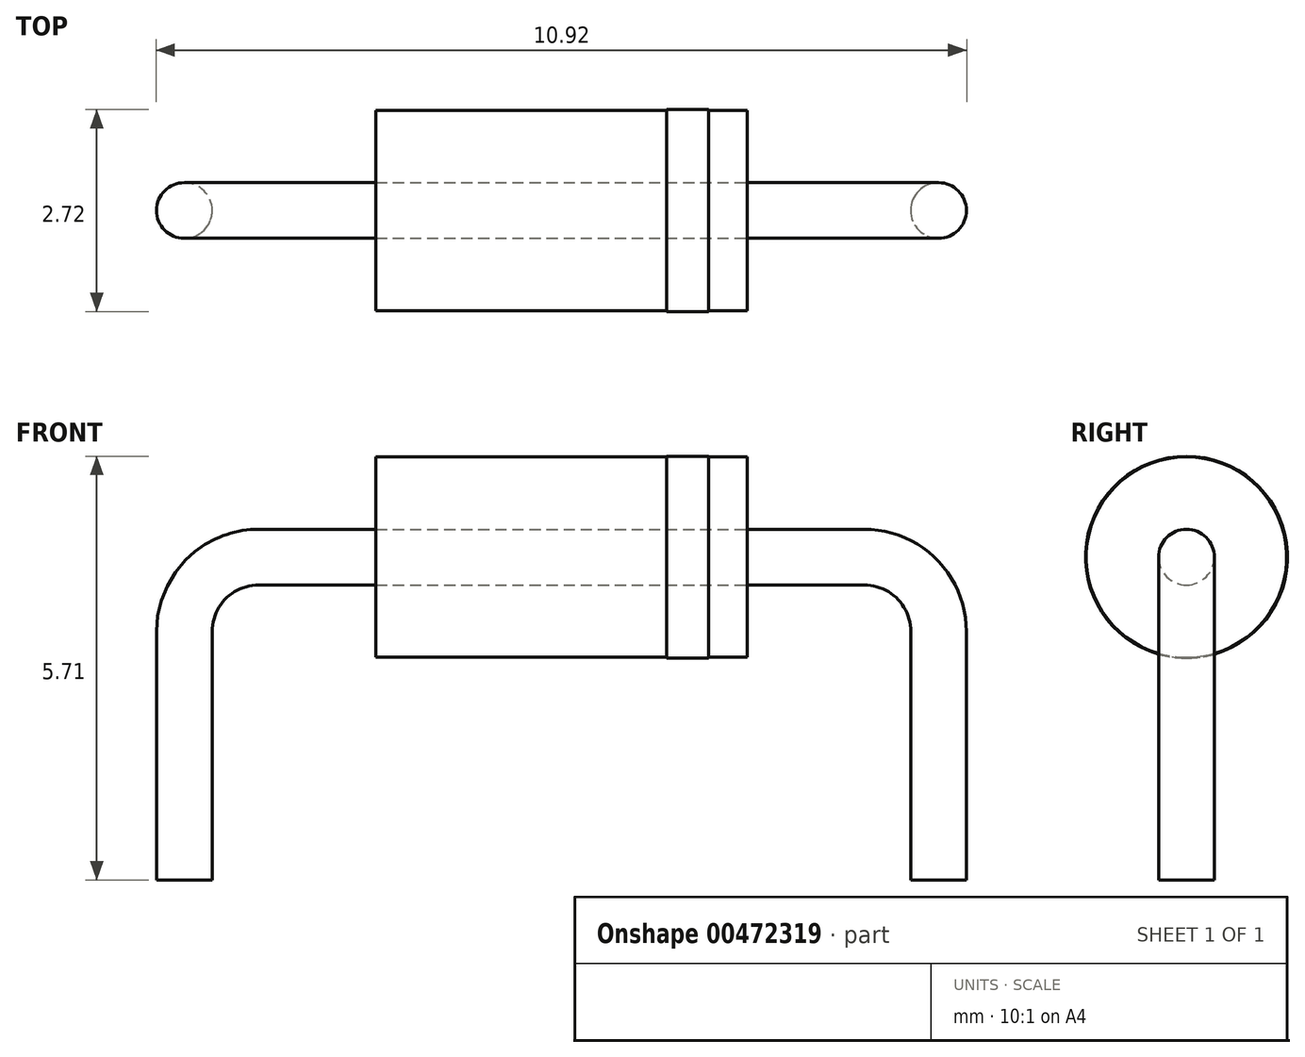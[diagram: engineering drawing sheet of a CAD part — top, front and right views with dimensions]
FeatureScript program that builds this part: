
annotation { "Feature Type Name" : "Feature", "Feature Type Description" : "" }
export const myFeature = defineFeature(function(context is Context, id is Id, definition is map)
    precondition{}
    {
        {
            var Q0;
            Q0=qCreatedBy(makeId("Front.planeOp"),FACE);
            var sketch = newSketch(context, id + "F0", { "sketchPlane" : qUnion([Q0])});
            skLineSegment(sketch, "E0", {"start": v(-5.08, 0) * mm, "end": v(-5.08, 3.35) * mm});
            skLineSegment(sketch, "E1", {"start": v(-4.08, 4.35) * mm, "end": v(4.08, 4.35) * mm});
            skLineSegment(sketch, "E2", {"start": v(5.08, 3.35) * mm, "end": v(5.08, 0) * mm});
            skPoint(sketch, "E3.visualSharp", {"position": v(-5.08, 4.35) * mm});
            skArc(sketch, "E3.filletArc", {"start": v(-4.08, 4.35) * mm, "mid": v(-4.79, 4.06) * mm, "end": v(-5.08, 3.35) * mm});
            skPoint(sketch, "E4.visualSharp", {"position": v(5.08, 4.35) * mm});
            skArc(sketch, "E4.filletArc", {"start": v(5.08, 3.35) * mm, "mid": v(4.79, 4.06) * mm, "end": v(4.08, 4.35) * mm});
            skSolve(sketch);
        }
        {
            var Q0;
            Q0=qCreatedBy(makeId("Top.planeOp"),FACE);
            var sketch = newSketch(context, id + "F1", { "sketchPlane" : qUnion([Q0])});
            skCircle(sketch, "E5", {"center": v(-5.08, 0) * mm, "radius": 0.38 * mm});
            skSolve(sketch);
        }
        {
            var Q0;
            Q0=qSketchRegion(id+"F1",true);
            var Q1;
            Q1=qConstructionFilter(qBodyType(qCreatedBy(id+"F0",EDGE),BodyType.WIRE),ConstructionObject.NO);
            sweep(context, id + "F2", {"profiles" : qUnion([Q0]), "path" : qUnion([Q1])});
        }
        {
            var Q0;
            Q0=qCreatedBy(makeId("Right.planeOp"),FACE);
            var sketch = newSketch(context, id + "F3", { "sketchPlane" : qUnion([Q0])});
            skCircle(sketch, "E6", {"center": v(0, 4.35) * mm, "radius": 1.35 * mm});
            skSolve(sketch);
        }
        {
            var Q0;
            Q0=makeQuery(id+"F3.imprint","IMPRINT",FACE,{"disambiguationData":[TD([[makeQuery(id+"F3.imprint","IMPRINT",EDGE,{"derivedFrom":sQuery(id+"F3.wireOp",EDGE,"E6")}),1.0]])]});
            extrude(context, id + "F4", {"entities" : qUnion([Q0]), "oppositeDirection" : true, "depth" : 2.5 * mm, "hasSecondDirection" : true, "secondDirectionOppositeDirection" : false, "secondDirectionDepth" : 2.5 * mm});
        }
        {
            var Q0;
            Q0=makeQuery(id+"F4.opExtrude","CAP_FACE",FACE,{"disambiguationData":[OSD([sQuery(id+"F3.wireOp",EDGE,"E6")])],"isStart":true});
            var sketch = newSketch(context, id + "F5", { "sketchPlane" : qUnion([Q0])});
            skCircle(sketch, "E7", {"center": v(0, 4.35) * mm, "radius": 1.36 * mm});
            skSolve(sketch);
        }
        {
            var Q0;
            Q0=qSketchRegion(id+"F5",true);
            extrude(context, id + "F6", {"entities" : qUnion([Q0]), "oppositeDirection" : true, "depth" : 1.08 * mm, "hasSecondDirection" : true, "secondDirectionOppositeDirection" : true, "secondDirectionDepth" : 0.52 * mm});
        }
    });
